FCSTD DOCUMENT  (FreeCAD 0.20R29177 (Git))
Label: Studs_Hub
License: All rights reserved
LicenseURL: http://en.wikipedia.org/wiki/All_rights_reserved
objects: App::Link×1, Part::FeaturePython×1, Spreadsheet::Sheet×1
EXTERNAL_REF file=Studs_Hub_Base.FCStd obj=Part
EXTERNAL_REF file=../../Master_of_Puppets.FCStd obj=Hub
EXTERNAL_REF file=../../Master_of_Puppets.FCStd obj=Spreadsheet

FEATURE [App::Link] Link  label="Base"
  LinkPlacement = pos=(0,50,0) rot=(0,0,1;0rad)
  LinkedObject = -> <external Studs_Hub_Base.FCStd>#Part
  Placement = pos=(0,50,0) rot=(0,0,1;0rad)
  expr: .Placement.Base.y = Spreadsheet.HubPitchCircleRadius
FEATURE [Part::FeaturePython] Array  label="Studs_Hub"  # Draft array (typed FeaturePython)
  AlwaysSyncPlacement = false
  Angle = 360
  ArrayType = 1
  Axis = (0,0,1)
  Base = -> Link
  Center = (0,0,0)
  Count = 4
  ExpandArray = false
  Fuse = false
  IntervalAxis = (0,0,0)
  IntervalX = (50,0,0)
  IntervalY = (0,50,0)
  IntervalZ = (0,0,50)
  NumberCircles = 3
  NumberPolar = 4
  NumberX = 2
  NumberY = 2
  NumberZ = 1
  PlacementList = 4 placements: [(0,50,0),(-50,1.42109e-14,0),(-6.12323e-15,-50,0),(50,-1.42109e-14,0)]
  RadialDistance = 50
  ScaleList = (4) [(1,1,1),(1,1,1),(1,1,1),(1,1,1)]
  Symmetry = 1
  TangentialDistance = 25
  expr: NumberPolar = Spreadsheet.NumberOfStuds
FEATURE [Spreadsheet::Sheet] Spreadsheet
  cells = A1=Inputs; A2=HubPitchCircleRadius; B2(HubPitchCircleRadius)==Master_of_Puppets#Hub.HubPitchCircleRadius; A3=RotorDiskRadius; B3(RotorDiskRadius)==Master_of_Puppets#Spreadsheet.RotorDiskRadius; A4=NumberOfHoles; B4(NumberOfHoles)==Master_of_Puppets#Hub.NumberOfHoles; A5=NumberOfStuds; B5(NumberOfStuds)==NumberOfHoles
